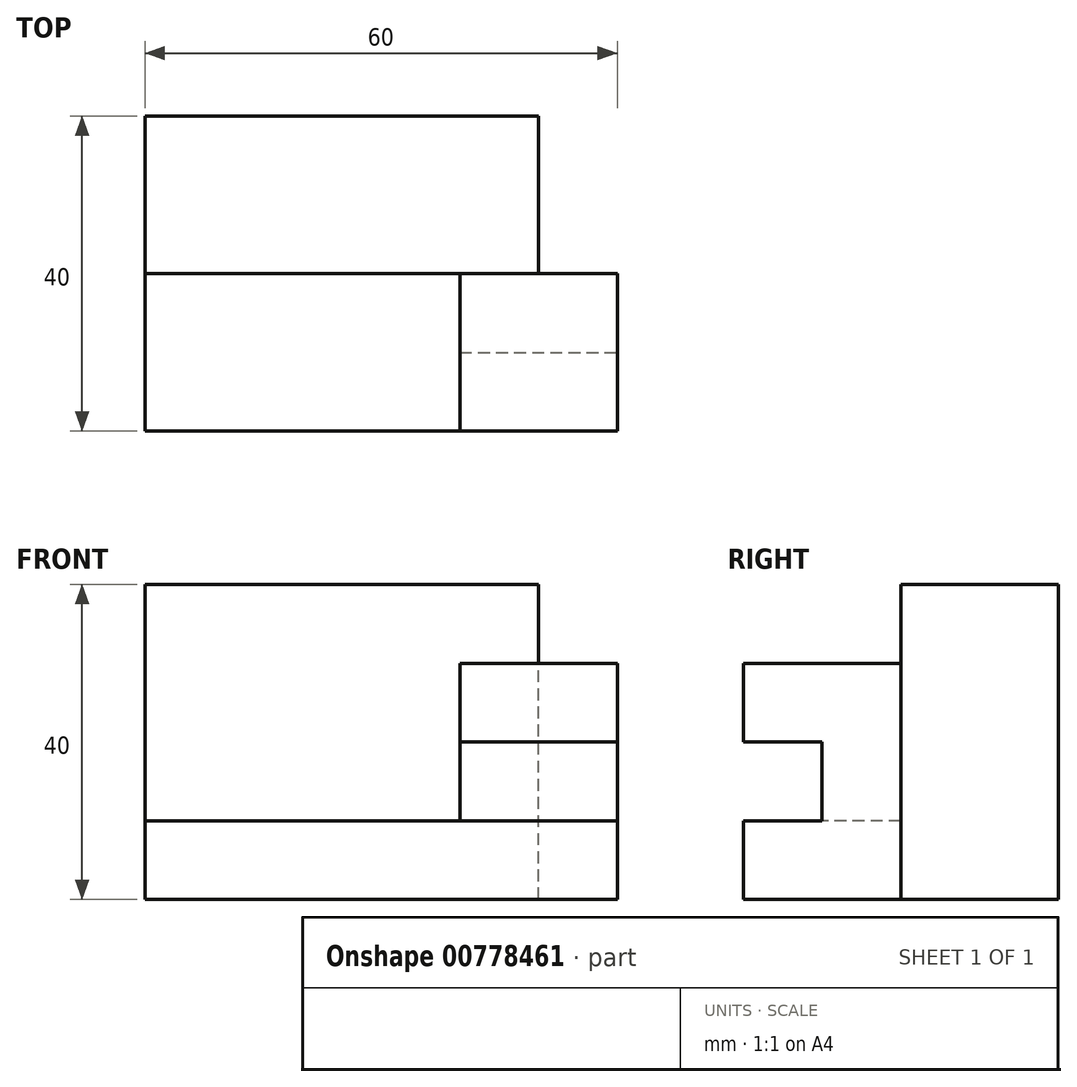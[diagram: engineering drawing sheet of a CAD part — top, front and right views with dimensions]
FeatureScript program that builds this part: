
annotation { "Feature Type Name" : "Feature", "Feature Type Description" : "" }
export const myFeature = defineFeature(function(context is Context, id is Id, definition is map)
    precondition{}
    {
        {
            var Q0;
            Q0=qCreatedBy(makeId("Front.planeOp"),FACE);
            var sketch = newSketch(context, id + "F0", { "sketchPlane" : qUnion([Q0])});
            skLineSegment(sketch, "E0", {"start": v(0, 0) * mm, "end": v(60, 0) * mm});
            skLineSegment(sketch, "E1", {"start": v(60, 0) * mm, "end": v(60, 40) * mm});
            skLineSegment(sketch, "E2", {"start": v(60, 40) * mm, "end": v(0, 40) * mm});
            skLineSegment(sketch, "E3", {"start": v(0, 40) * mm, "end": v(0, 0) * mm});
            skSolve(sketch);
        }
        {
            var Q0;
            Q0 = qSketchRegion(id + "F0", true);
            extrude(context, id + "F1", {"entities" : qUnion([Q0]), "depth" : 40 * mm, "offsetDistance" : 25 * mm});
        }
        {
            var Q0;
            Q0=makeQuery(id+"F1.opExtrude","SWEPT_FACE",FACE,{"disambiguationData":[OSD([sQuery(id+"F0.wireOp",EDGE,"E1")])]});
            var sketch = newSketch(context, id + "F2", { "sketchPlane" : qUnion([Q0])});
            skLineSegment(sketch, "E4", {"start": v(0, 0) * mm, "end": v(-20, 0) * mm});
            skLineSegment(sketch, "E5", {"start": v(-20, 0) * mm, "end": v(-20, 40) * mm});
            skLineSegment(sketch, "E6", {"start": v(-20, 40) * mm, "end": v(0, 40) * mm});
            skLineSegment(sketch, "E7", {"start": v(0, 40) * mm, "end": v(0, 0) * mm});
            skLineSegment(sketch, "E8", {"start": v(-20, 40) * mm, "end": v(-40, 40) * mm});
            skLineSegment(sketch, "E9", {"start": v(-40, 40) * mm, "end": v(-40, 30) * mm});
            skLineSegment(sketch, "E10", {"start": v(-40, 30) * mm, "end": v(-20, 30) * mm});
            skLineSegment(sketch, "E11", {"start": v(-20, 30) * mm, "end": v(-20, 40) * mm});
            skSolve(sketch);
        }
        {
            var Q0;
            Q0=makeQuery(id+"F2.imprint","IMPRINT",FACE,{"disambiguationData":[TD([[makeQuery(id+"F2.imprint","IMPRINT",EDGE,{"derivedFrom":sQuery(id+"F2.wireOp",EDGE,"E8")}),-1.0]])]});
            extrude(context, id + "F3", {"entities" : qUnion([Q0]), "operationType" : NewBodyOperationType.REMOVE, "oppositeDirection" : true, "depth" : 60 * mm, "offsetDistance" : 25 * mm});
        }
        {
            var Q0;
            Q0=makeQuery(id+"F2.imprint","IMPRINT",FACE,{"disambiguationData":[TD([[makeQuery(id+"F2.imprint","IMPRINT",EDGE,{"derivedFrom":sQuery(id+"F2.wireOp",EDGE,"E4")}),1.0]])]});
            extrude(context, id + "F4", {"entities" : qUnion([Q0]), "operationType" : NewBodyOperationType.REMOVE, "oppositeDirection" : true, "depth" : 10 * mm, "offsetDistance" : 25 * mm});
        }
        {
            var Q0;
            Q0=makeQuery(id+"F1.opExtrude","CAP_FACE",FACE,{"disambiguationData":[OSD([sQuery(id+"F0.wireOp",EDGE,"E0"),sQuery(id+"F0.wireOp",EDGE,"E1"),sQuery(id+"F0.wireOp",EDGE,"E2"),sQuery(id+"F0.wireOp",EDGE,"E3")])],"isStart":false});
            var sketch = newSketch(context, id + "F5", { "sketchPlane" : qUnion([Q0])});
            skLineSegment(sketch, "E12", {"start": v(0, 0) * mm, "end": v(0, 10) * mm});
            skLineSegment(sketch, "E13", {"start": v(0, 10) * mm, "end": v(40, 10) * mm});
            skLineSegment(sketch, "E14", {"start": v(40, 10) * mm, "end": v(40, 30) * mm});
            skLineSegment(sketch, "E15", {"start": v(40, 30) * mm, "end": v(0, 30) * mm});
            skLineSegment(sketch, "E16", {"start": v(0, 30) * mm, "end": v(0, 0) * mm});
            skSolve(sketch);
        }
        {
            var Q0;
            Q0 = qSketchRegion(id + "F5", true);
            extrude(context, id + "F6", {"entities" : qUnion([Q0]), "operationType" : NewBodyOperationType.REMOVE, "oppositeDirection" : true, "depth" : 20 * mm, "offsetDistance" : 25 * mm});
        }
        {
            var Q0;
            Q0=makeQuery(id+"F1.opExtrude","SWEPT_FACE",FACE,{"disambiguationData":[OSD([sQuery(id+"F0.wireOp",EDGE,"E1")])]});
            var sketch = newSketch(context, id + "F7", { "sketchPlane" : qUnion([Q0])});
            skLineSegment(sketch, "E17", {"start": v(-40, 30) * mm, "end": v(-40, 20) * mm});
            skLineSegment(sketch, "E18", {"start": v(-40, 20) * mm, "end": v(-30, 20) * mm});
            skLineSegment(sketch, "E19", {"start": v(-30, 20) * mm, "end": v(-30, 10) * mm});
            skLineSegment(sketch, "E20", {"start": v(-30, 10) * mm, "end": v(-40, 10) * mm});
            skLineSegment(sketch, "E21", {"start": v(-40, 10) * mm, "end": v(-40, 20) * mm});
            skSolve(sketch);
        }
        {
            var Q0;
            Q0 = qSketchRegion(id + "F7", true);
            extrude(context, id + "F8", {"entities" : qUnion([Q0]), "operationType" : NewBodyOperationType.REMOVE, "oppositeDirection" : true, "depth" : 20 * mm, "offsetDistance" : 25 * mm});
        }
    });
